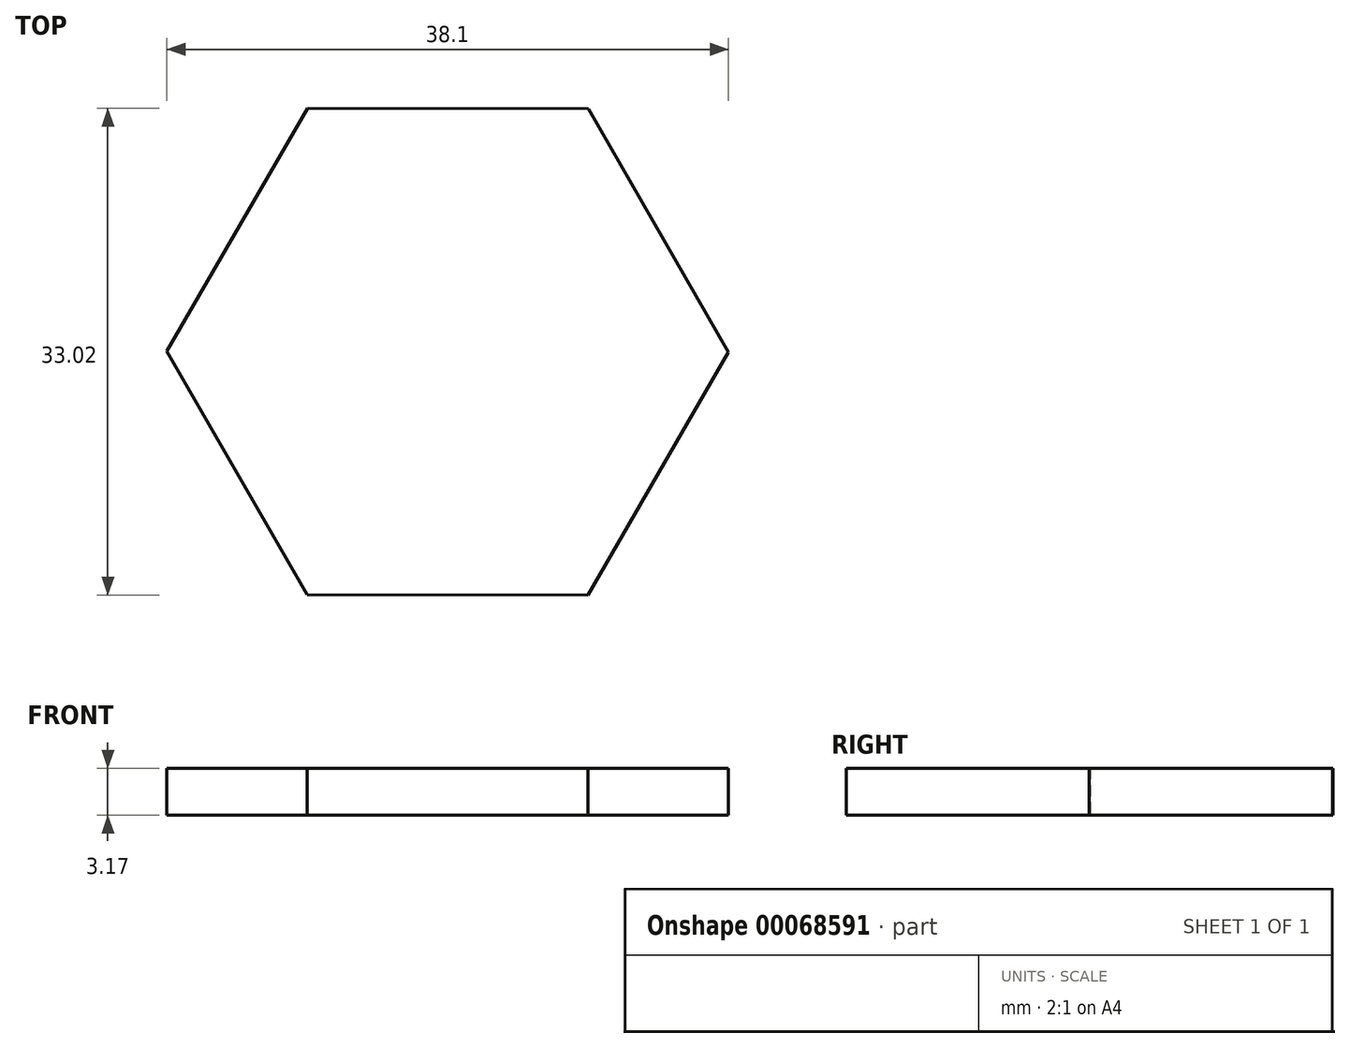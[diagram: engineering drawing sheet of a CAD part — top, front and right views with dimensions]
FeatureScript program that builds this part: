
annotation { "Feature Type Name" : "Feature", "Feature Type Description" : "" }
export const myFeature = defineFeature(function(context is Context, id is Id, definition is map)
    precondition{}
    {
        {
            var Q0;
            Q0=qCreatedBy(makeId("Top.planeOp"),FACE);
            var sketch = newSketch(context, id + "F0", { "sketchPlane" : qUnion([Q0])});
            skCircle(sketch, "E0.cCircle", {"center": v(0, 0) * mm, "radius": 16.5 * mm, "construction": true});
            skLineSegment(sketch, "E0.0", {"start": v(9.54, 16.49) * mm, "end": v(19.05, -0.02) * mm});
            skLineSegment(sketch, "E0.1", {"start": v(19.05, -0.02) * mm, "end": v(9.5, -16.5) * mm});
            skLineSegment(sketch, "E0.2", {"start": v(9.5, -16.5) * mm, "end": v(-9.54, -16.49) * mm});
            skLineSegment(sketch, "E0.3", {"start": v(-9.54, -16.49) * mm, "end": v(-19.05, 0.02) * mm});
            skLineSegment(sketch, "E0.4", {"start": v(-19.05, 0.02) * mm, "end": v(-9.5, 16.5) * mm});
            skLineSegment(sketch, "E0.5", {"start": v(-9.5, 16.5) * mm, "end": v(9.54, 16.49) * mm});
            skPoint(sketch, "E0.0.midPoint", {"position": v(14.3, 8.23) * mm});
            skSolve(sketch);
        }
        {
            var Q0;
            Q0=makeQuery(id+"F0.imprint","IMPRINT",FACE,{"disambiguationData":[TD([[makeQuery(id+"F0.imprint","IMPRINT",EDGE,{"derivedFrom":sQuery(id+"F0.wireOp",EDGE,"E0.0")}),-1.0]])]});
            extrude(context, id + "F1", {"entities" : qUnion([Q0]), "depth" : 3.17 * mm});
        }
    });
